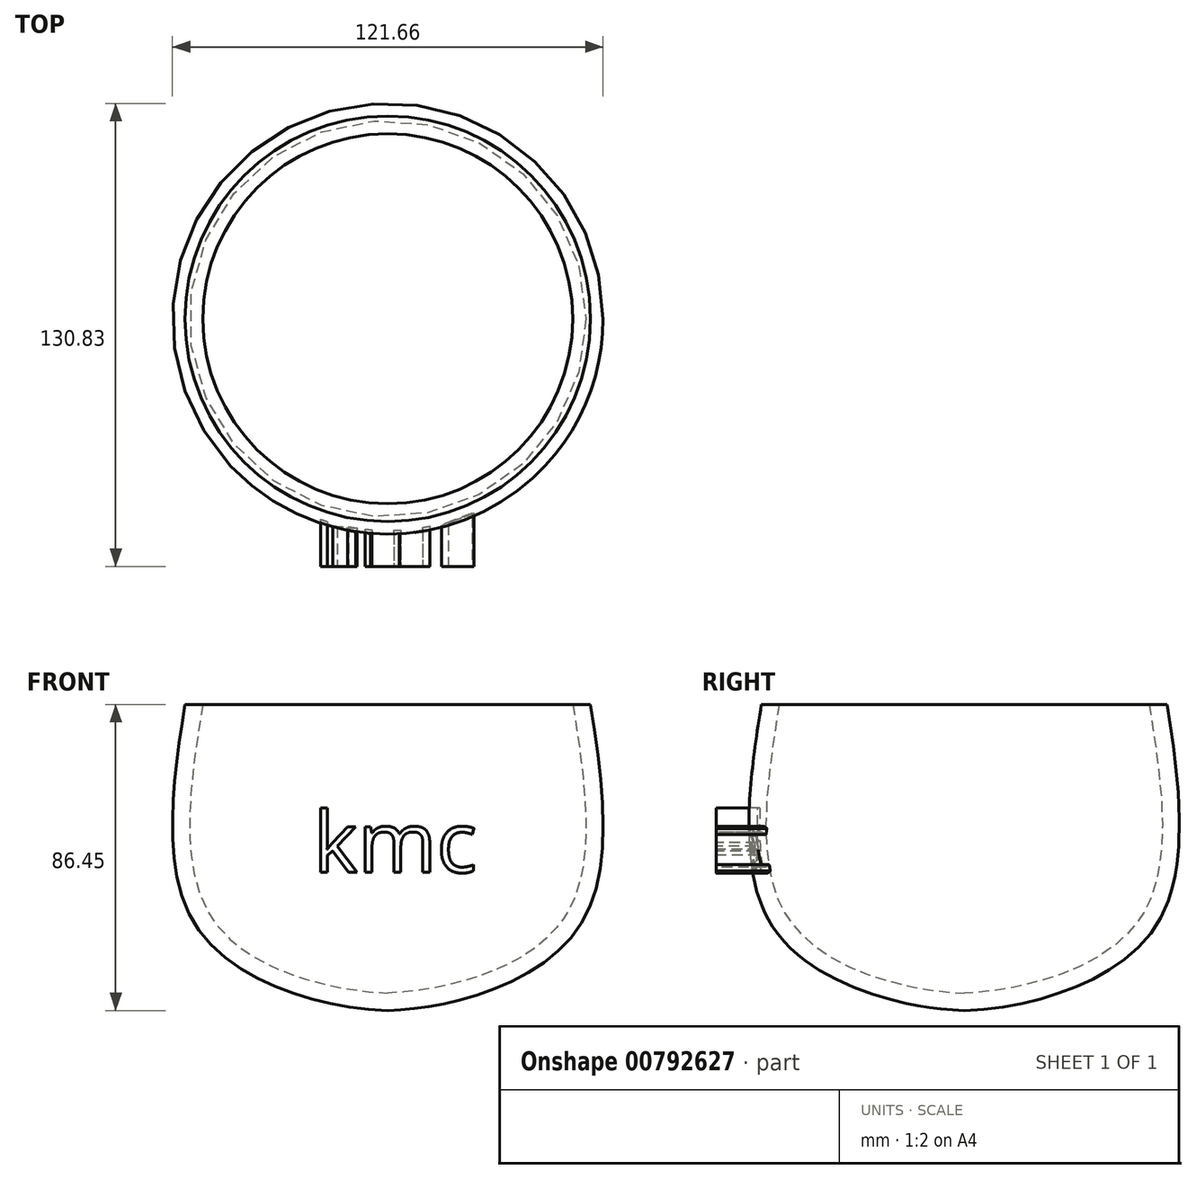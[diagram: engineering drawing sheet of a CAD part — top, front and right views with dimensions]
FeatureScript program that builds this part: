
annotation { "Feature Type Name" : "Feature", "Feature Type Description" : "" }
export const myFeature = defineFeature(function(context is Context, id is Id, definition is map)
    precondition{}
    {
        {
            var Q0;
            Q0=qCreatedBy(makeId("Front.planeOp"),FACE);
            var sketch = newSketch(context, id + "F0", { "sketchPlane" : qUnion([Q0])});
            skFitSpline(sketch, "E0", {"points": [v(55.5, 48.93) * mm, v(54.63, -23.48) * mm, v(15.14, -46.3) * mm, v(-10.31, -48.05) * mm], "startDerivative": vector(34.03, -198.61) * mm, "endDerivative": vector(-92.7, 1.74) * mm});
            skFitSpline(sketch, "E1.0", {"points": [v(50.58, 48.08) * mm, v(51.29, 43.94) * mm, v(52.7, 35.7) * mm, v(54.5, 23.66) * mm, v(55.7, 12.18) * mm, v(56, 1.52) * mm, v(55.3, -6.46) * mm, v(54.07, -12.16) * mm, v(52.8, -16.07) * mm, v(51.46, -19.01) * mm, v(50.2, -21.18) * mm, v(48.79, -23.25) * mm, v(46.75, -25.69) * mm, v(42.97, -29.27) * mm, v(37.36, -33.16) * mm, v(29.75, -36.86) * mm, v(23.14, -39.16) * mm, v(17.99, -40.56) * mm, v(14.26, -41.4) * mm, v(10.77, -42.03) * mm, v(6.37, -42.65) * mm, v(1.28, -43.06) * mm, v(-4.49, -43.16) * mm, v(-8.29, -43.09) * mm, v(-10.22, -43.05) * mm]});
            skLineSegment(sketch, "E2", {"start": v(0, -14.26) * mm, "end": v(0, -71.3) * mm});
            skLineSegment(sketch, "E3", {"start": v(34.45, 38.4) * mm, "end": v(74.82, 38.4) * mm});
            skSolve(sketch);
        }
        {
            var Q0;
            {var subQ0=sQuery(id+"F0.wireOp",EDGE,"E2");var subQ1=sQuery(id+"F0.wireOp",EDGE,"E0");var subQ2=makeQuery(id+"F0.imprint","INTERSECT",VERTEX,{"derivedFrom":[subQ1,subQ0]});Q0=makeQuery(id+"F0.imprint","IMPRINT",FACE,{"disambiguationData":[TD([[makeQuery(id+"F0.imprint","IMPRINT",EDGE,{"disambiguationData":[TD([[subQ2,1.0]])],"derivedFrom":subQ1}),-1.0]])]});}
            var Q1;
            Q1=sQuery(id+"F0.wireOp",EDGE,"E2");
            revolve(context, id + "F1", {"surfaceOperationType" : NewSurfaceOperationType.NEW, "entities" : qUnion([Q0]), "axis" : qUnion([Q1]), "revolveType" : RevolveType.FULL});
        }
        {
            var Q0;
            Q0=qCreatedBy(makeId("Front.planeOp"),FACE);
            cPlane(context, id + "F2", {"entities" : qUnion([Q0]), "cplaneType" : CPlaneType.OFFSET, "offset" : 70 * mm, "width" : 150 * mm, "height" : 150 * mm});
        }
        {
            var Q0;
            Q0=qCreatedBy(id+"F2.planeOp",FACE);
            var sketch = newSketch(context, id + "F3", { "sketchPlane" : qUnion([Q0])});
            skText(sketch, "E4", { "text": "kmc\n", "fontName": "OpenSans-Regular.ttf"});
            const initialGuessF3  = {"E4": [-0.02103, -0.00901, 1, 0, 0.01723]};
            skSetInitialGuess(sketch, initialGuessF3);
            skSolve(sketch);
        }
        {
            var Q0;
            Q0 = qSketchRegion(id + "F3", true);
            extrude(context, id + "F4", {"entities" : qUnion([Q0]), "operationType" : NewBodyOperationType.ADD, "endBound" : BoundingType.UP_TO_NEXT, "oppositeDirection" : true, "depth" : 25 * mm, "offsetDistance" : 25 * mm});
        }
    });
